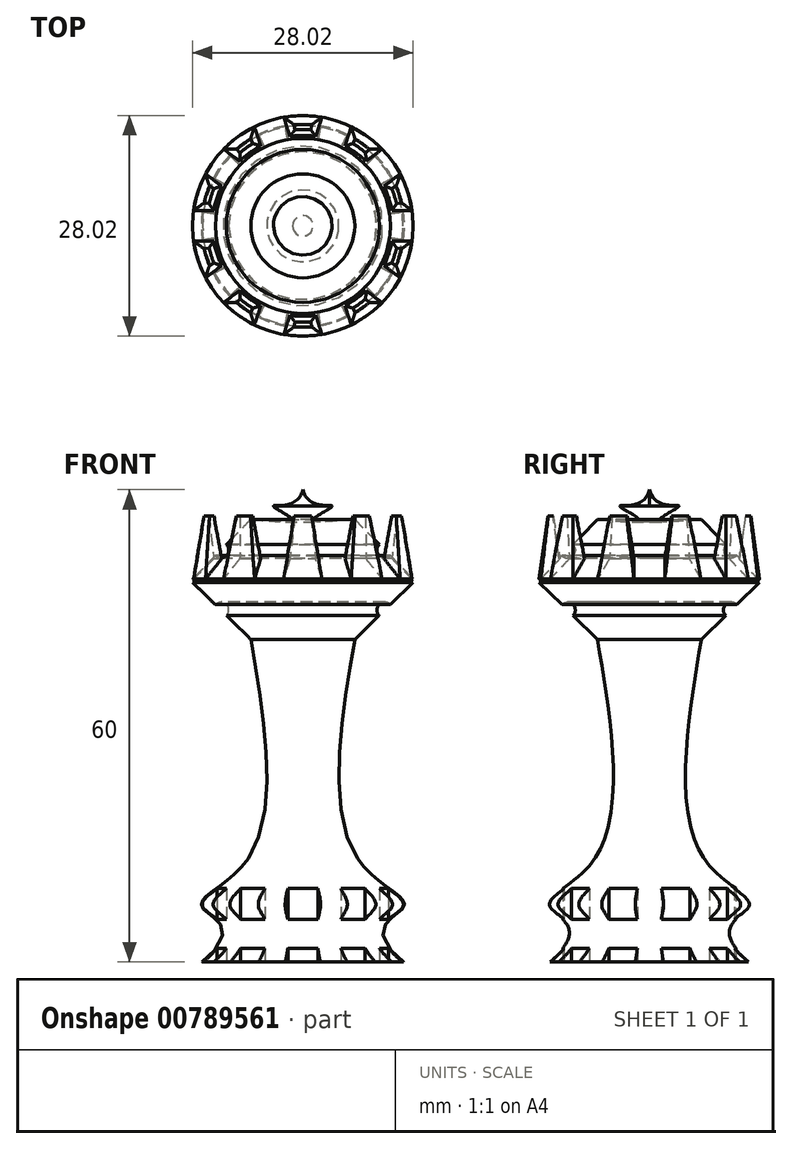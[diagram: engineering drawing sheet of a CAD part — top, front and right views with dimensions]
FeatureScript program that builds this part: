
annotation { "Feature Type Name" : "Feature", "Feature Type Description" : "" }
export const myFeature = defineFeature(function(context is Context, id is Id, definition is map)
    precondition{}
    {
        {
            var Q0;
            Q0=qCreatedBy(makeId("Front.planeOp"),FACE);
            var sketch = newSketch(context, id + "F0", { "sketchPlane" : qUnion([Q0])});
            skLineSegment(sketch, "E0", {"start": v(0, 0) * mm, "end": v(0, 60) * mm});
            skLineSegment(sketch, "E1", {"start": v(-2.2, 0) * mm, "end": v(12.8, 0) * mm});
            skFitSpline(sketch, "E2", {"points": [v(12.8, 0) * mm, v(12.8, 6.96) * mm, v(7.52, 12.35) * mm, v(6.6, 41) * mm], "startDerivative": vector(-68.04, 55.14) * mm, "endDerivative": vector(13.36, 76.17) * mm});
            skLineSegment(sketch, "E3", {"start": v(6.6, 41) * mm, "end": v(11.13, 45.4) * mm});
            skLineSegment(sketch, "E4", {"start": v(14.01, 48.63) * mm, "end": v(6.6, 56.23) * mm});
            skCircle(sketch, "E5", {"center": v(10.41, 52.32) * mm, "radius": 1 * mm});
            skCircle(sketch, "E6", {"center": v(10.41, 44.7) * mm, "radius": 1 * mm});
            skLineSegment(sketch, "E7", {"start": v(14.01, 48.63) * mm, "end": v(12.73, 48.41) * mm});
            skLineSegment(sketch, "E8", {"start": v(12.73, 48.41) * mm, "end": v(14, 48.2) * mm});
            skPoint(sketch, "E9.orphan", {"position": v(14.22, 48.41) * mm});
            skLineSegment(sketch, "E10", {"start": v(14, 48.2) * mm, "end": v(11.13, 45.4) * mm});
            skFitSpline(sketch, "E11", {"points": [v(3.74, 57.92) * mm, v(4.88, 57.03) * mm, v(3.83, 56) * mm], "startDerivative": vector(3.37, -1.72) * mm, "endDerivative": vector(-3.17, -2.1) * mm});
            skFitSpline(sketch, "E12.trimOffspring", {"points": [v(6.6, 56.23) * mm, v(1.34, 56.23) * mm, v(3.74, 57.92) * mm, v(0, 60) * mm], "startDerivative": vector(-22.01, -1.8) * mm, "endDerivative": vector(-5.75, 23.43) * mm});
            skFitSpline(sketch, "E13", {"points": [v(4.7, 56.66) * mm, v(5.56, 56.61) * mm, v(6.6, 56.23) * mm], "startDerivative": vector(1.82, 0.06) * mm, "endDerivative": vector(2, -0.89) * mm});
            skSolve(sketch);
        }
        {
            var Q0;
            {var subQ2=sQuery(id+"F0.wireOp",EDGE,"E0");Q0=makeQuery(id+"F0.imprint","IMPRINT",FACE,{"disambiguationData":[TD([[makeQuery(id+"F0.imprint","IMPRINT",EDGE,{"derivedFrom":subQ2}),-1.0]])]});}
            var Q1;
            Q1=sQuery(id+"F0.wireOp",EDGE,"E0");
            revolve(context, id + "F1", {"surfaceOperationType" : NewSurfaceOperationType.NEW, "entities" : qUnion([Q0]), "axis" : qUnion([Q1]), "revolveType" : RevolveType.FULL});
        }
        {
            var Q0;
            Q0=qCreatedBy(makeId("Top.planeOp"),FACE);
            var sketch = newSketch(context, id + "F2", { "sketchPlane" : qUnion([Q0])});
            skLineSegment(sketch, "E14", {"start": v(2.43, -13.79) * mm, "end": v(1.91, -10.83) * mm});
            skLineSegment(sketch, "E15", {"start": v(-1.91, -10.83) * mm, "end": v(-2.43, -13.79) * mm});
            skArc(sketch, "E16", {"start": v(-2.43, -13.79) * mm, "mid": v(0, -14) * mm, "end": v(2.43, -13.79) * mm});
            skArc(sketch, "E17", {"start": v(-1.91, -10.83) * mm, "mid": v(0, -11) * mm, "end": v(1.91, -10.83) * mm});
            skPoint(sketch, "E18.orphan", {"position": v(0, -22.16) * mm});
            skPoint(sketch, "E19.orphan", {"position": v(-3.9, -22.16) * mm});
            skArc(sketch, "E20.1.0", {"start": v(6.14, -12.58) * mm, "mid": v(8.23, -11.33) * mm, "end": v(10.07, -9.73) * mm});
            skLineSegment(sketch, "E20.1.1", {"start": v(4.82, -9.89) * mm, "end": v(6.14, -12.58) * mm});
            skArc(sketch, "E20.1.2", {"start": v(4.82, -9.89) * mm, "mid": v(6.47, -8.9) * mm, "end": v(7.91, -7.64) * mm});
            skLineSegment(sketch, "E20.1.3", {"start": v(10.07, -9.73) * mm, "end": v(7.91, -7.64) * mm});
            skArc(sketch, "E20.2.0", {"start": v(12.36, -6.57) * mm, "mid": v(13.31, -4.33) * mm, "end": v(13.86, -1.95) * mm});
            skLineSegment(sketch, "E20.2.1", {"start": v(9.71, -5.16) * mm, "end": v(12.36, -6.57) * mm});
            skArc(sketch, "E20.2.2", {"start": v(9.71, -5.16) * mm, "mid": v(10.46, -3.4) * mm, "end": v(10.9, -1.53) * mm});
            skLineSegment(sketch, "E20.2.3", {"start": v(13.86, -1.95) * mm, "end": v(10.9, -1.53) * mm});
            skArc(sketch, "E20.3.0", {"start": v(13.86, 1.95) * mm, "mid": v(13.31, 4.33) * mm, "end": v(12.36, 6.57) * mm});
            skLineSegment(sketch, "E20.3.1", {"start": v(10.9, 1.53) * mm, "end": v(13.86, 1.95) * mm});
            skArc(sketch, "E20.3.2", {"start": v(10.9, 1.53) * mm, "mid": v(10.46, 3.4) * mm, "end": v(9.71, 5.16) * mm});
            skLineSegment(sketch, "E20.3.3", {"start": v(12.36, 6.57) * mm, "end": v(9.71, 5.16) * mm});
            skArc(sketch, "E20.4.0", {"start": v(10.07, 9.73) * mm, "mid": v(8.23, 11.33) * mm, "end": v(6.14, 12.58) * mm});
            skLineSegment(sketch, "E20.4.1", {"start": v(7.91, 7.64) * mm, "end": v(10.07, 9.73) * mm});
            skArc(sketch, "E20.4.2", {"start": v(7.91, 7.64) * mm, "mid": v(6.47, 8.9) * mm, "end": v(4.82, 9.89) * mm});
            skLineSegment(sketch, "E20.4.3", {"start": v(6.14, 12.58) * mm, "end": v(4.82, 9.89) * mm});
            skArc(sketch, "E20.5.0", {"start": v(2.43, 13.79) * mm, "mid": v(0, 14) * mm, "end": v(-2.43, 13.79) * mm});
            skLineSegment(sketch, "E20.5.1", {"start": v(1.91, 10.83) * mm, "end": v(2.43, 13.79) * mm});
            skArc(sketch, "E20.5.2", {"start": v(1.91, 10.83) * mm, "mid": v(0, 11) * mm, "end": v(-1.91, 10.83) * mm});
            skLineSegment(sketch, "E20.5.3", {"start": v(-2.43, 13.79) * mm, "end": v(-1.91, 10.83) * mm});
            skArc(sketch, "E20.6.0", {"start": v(-6.14, 12.58) * mm, "mid": v(-8.23, 11.33) * mm, "end": v(-10.07, 9.73) * mm});
            skLineSegment(sketch, "E20.6.1", {"start": v(-4.82, 9.89) * mm, "end": v(-6.14, 12.58) * mm});
            skArc(sketch, "E20.6.2", {"start": v(-4.82, 9.89) * mm, "mid": v(-6.47, 8.9) * mm, "end": v(-7.91, 7.64) * mm});
            skLineSegment(sketch, "E20.6.3", {"start": v(-10.07, 9.73) * mm, "end": v(-7.91, 7.64) * mm});
            skArc(sketch, "E20.7.0", {"start": v(-12.36, 6.57) * mm, "mid": v(-13.31, 4.33) * mm, "end": v(-13.86, 1.95) * mm});
            skLineSegment(sketch, "E20.7.1", {"start": v(-9.71, 5.16) * mm, "end": v(-12.36, 6.57) * mm});
            skArc(sketch, "E20.7.2", {"start": v(-9.71, 5.16) * mm, "mid": v(-10.46, 3.4) * mm, "end": v(-10.9, 1.53) * mm});
            skLineSegment(sketch, "E20.7.3", {"start": v(-13.86, 1.95) * mm, "end": v(-10.9, 1.53) * mm});
            skArc(sketch, "E20.8.0", {"start": v(-13.86, -1.95) * mm, "mid": v(-13.31, -4.33) * mm, "end": v(-12.36, -6.57) * mm});
            skLineSegment(sketch, "E20.8.1", {"start": v(-10.9, -1.53) * mm, "end": v(-13.86, -1.95) * mm});
            skArc(sketch, "E20.8.2", {"start": v(-10.9, -1.53) * mm, "mid": v(-10.46, -3.4) * mm, "end": v(-9.71, -5.16) * mm});
            skLineSegment(sketch, "E20.8.3", {"start": v(-12.36, -6.57) * mm, "end": v(-9.71, -5.16) * mm});
            skArc(sketch, "E20.9.0", {"start": v(-10.07, -9.73) * mm, "mid": v(-8.23, -11.33) * mm, "end": v(-6.14, -12.58) * mm});
            skLineSegment(sketch, "E20.9.1", {"start": v(-7.91, -7.64) * mm, "end": v(-10.07, -9.73) * mm});
            skArc(sketch, "E20.9.2", {"start": v(-7.91, -7.64) * mm, "mid": v(-6.47, -8.9) * mm, "end": v(-4.82, -9.89) * mm});
            skLineSegment(sketch, "E20.9.3", {"start": v(-6.14, -12.58) * mm, "end": v(-4.82, -9.89) * mm});
            skSolve(sketch);
        }
        {
            var Q0;
            Q0=qCreatedBy(makeId("Top.planeOp"),FACE);
            cPlane(context, id + "F3", {"entities" : qUnion([Q0]), "cplaneType" : CPlaneType.OFFSET, "offset" : 48.62 * mm, "width" : 150 * mm, "height" : 150 * mm});
        }
        {
            var Q0;
            Q0=qCreatedBy(id+"F3.planeOp",FACE);
            var sketch = newSketch(context, id + "F4", { "sketchPlane" : qUnion([Q0])});
            skArc(sketch, "E21", {"start": v(2.43, 13.79) * mm, "mid": v(0, 14) * mm, "end": v(-2.43, 13.79) * mm});
            skArc(sketch, "E22", {"start": v(1.93, 10.94) * mm, "mid": v(0, 11.11) * mm, "end": v(-1.93, 10.94) * mm});
            skLineSegment(sketch, "E23", {"start": v(2.43, 13.79) * mm, "end": v(1.93, 10.94) * mm});
            skLineSegment(sketch, "E24", {"start": v(-1.93, 10.94) * mm, "end": v(-2.43, 13.79) * mm});
            skPoint(sketch, "E25.orphan", {"position": v(0, 20.43) * mm});
            skPoint(sketch, "E26.orphan", {"position": v(-3.6, 20.43) * mm});
            skArc(sketch, "E27.1.0", {"start": v(-6.14, 12.58) * mm, "mid": v(-8.23, 11.33) * mm, "end": v(-10.07, 9.73) * mm});
            skArc(sketch, "E27.1.1", {"start": v(-4.87, 9.99) * mm, "mid": v(-6.53, 9) * mm, "end": v(-8, 7.72) * mm});
            skLineSegment(sketch, "E27.1.2", {"start": v(-8, 7.72) * mm, "end": v(-10.07, 9.73) * mm});
            skLineSegment(sketch, "E27.1.3", {"start": v(-6.14, 12.58) * mm, "end": v(-4.87, 9.99) * mm});
            skArc(sketch, "E27.2.0", {"start": v(-12.36, 6.57) * mm, "mid": v(-13.31, 4.33) * mm, "end": v(-13.86, 1.95) * mm});
            skArc(sketch, "E27.2.1", {"start": v(-9.81, 5.22) * mm, "mid": v(-10.57, 3.43) * mm, "end": v(-11, 1.55) * mm});
            skLineSegment(sketch, "E27.2.2", {"start": v(-11, 1.55) * mm, "end": v(-13.86, 1.95) * mm});
            skLineSegment(sketch, "E27.2.3", {"start": v(-12.36, 6.57) * mm, "end": v(-9.81, 5.22) * mm});
            skArc(sketch, "E27.3.0", {"start": v(-13.86, -1.95) * mm, "mid": v(-13.31, -4.33) * mm, "end": v(-12.36, -6.57) * mm});
            skArc(sketch, "E27.3.1", {"start": v(-11, -1.55) * mm, "mid": v(-10.57, -3.43) * mm, "end": v(-9.81, -5.22) * mm});
            skLineSegment(sketch, "E27.3.2", {"start": v(-9.81, -5.22) * mm, "end": v(-12.36, -6.57) * mm});
            skLineSegment(sketch, "E27.3.3", {"start": v(-13.86, -1.95) * mm, "end": v(-11, -1.55) * mm});
            skArc(sketch, "E27.4.0", {"start": v(-10.07, -9.73) * mm, "mid": v(-8.23, -11.33) * mm, "end": v(-6.14, -12.58) * mm});
            skArc(sketch, "E27.4.1", {"start": v(-8, -7.72) * mm, "mid": v(-6.53, -9) * mm, "end": v(-4.87, -9.99) * mm});
            skLineSegment(sketch, "E27.4.2", {"start": v(-4.87, -9.99) * mm, "end": v(-6.14, -12.58) * mm});
            skLineSegment(sketch, "E27.4.3", {"start": v(-10.07, -9.73) * mm, "end": v(-8, -7.72) * mm});
            skArc(sketch, "E27.5.0", {"start": v(-2.43, -13.79) * mm, "mid": v(0, -14) * mm, "end": v(2.43, -13.79) * mm});
            skArc(sketch, "E27.5.1", {"start": v(-1.93, -10.94) * mm, "mid": v(0, -11.11) * mm, "end": v(1.93, -10.94) * mm});
            skLineSegment(sketch, "E27.5.2", {"start": v(1.93, -10.94) * mm, "end": v(2.43, -13.79) * mm});
            skLineSegment(sketch, "E27.5.3", {"start": v(-2.43, -13.79) * mm, "end": v(-1.93, -10.94) * mm});
            skArc(sketch, "E27.6.0", {"start": v(6.14, -12.58) * mm, "mid": v(8.23, -11.33) * mm, "end": v(10.07, -9.73) * mm});
            skArc(sketch, "E27.6.1", {"start": v(4.87, -9.99) * mm, "mid": v(6.53, -9) * mm, "end": v(8, -7.72) * mm});
            skLineSegment(sketch, "E27.6.2", {"start": v(8, -7.72) * mm, "end": v(10.07, -9.73) * mm});
            skLineSegment(sketch, "E27.6.3", {"start": v(6.14, -12.58) * mm, "end": v(4.87, -9.99) * mm});
            skArc(sketch, "E27.7.0", {"start": v(12.36, -6.57) * mm, "mid": v(13.31, -4.33) * mm, "end": v(13.86, -1.95) * mm});
            skArc(sketch, "E27.7.1", {"start": v(9.81, -5.22) * mm, "mid": v(10.57, -3.43) * mm, "end": v(11, -1.55) * mm});
            skLineSegment(sketch, "E27.7.2", {"start": v(11, -1.55) * mm, "end": v(13.86, -1.95) * mm});
            skLineSegment(sketch, "E27.7.3", {"start": v(12.36, -6.57) * mm, "end": v(9.81, -5.22) * mm});
            skArc(sketch, "E27.8.0", {"start": v(13.86, 1.95) * mm, "mid": v(13.31, 4.33) * mm, "end": v(12.36, 6.57) * mm});
            skArc(sketch, "E27.8.1", {"start": v(11, 1.55) * mm, "mid": v(10.57, 3.43) * mm, "end": v(9.81, 5.22) * mm});
            skLineSegment(sketch, "E27.8.2", {"start": v(9.81, 5.22) * mm, "end": v(12.36, 6.57) * mm});
            skLineSegment(sketch, "E27.8.3", {"start": v(13.86, 1.95) * mm, "end": v(11, 1.55) * mm});
            skArc(sketch, "E27.9.0", {"start": v(10.07, 9.73) * mm, "mid": v(8.23, 11.33) * mm, "end": v(6.14, 12.58) * mm});
            skArc(sketch, "E27.9.1", {"start": v(8, 7.72) * mm, "mid": v(6.53, 9) * mm, "end": v(4.87, 9.99) * mm});
            skLineSegment(sketch, "E27.9.2", {"start": v(4.87, 9.99) * mm, "end": v(6.14, 12.58) * mm});
            skLineSegment(sketch, "E27.9.3", {"start": v(10.07, 9.73) * mm, "end": v(8, 7.72) * mm});
            skSolve(sketch);
        }
        {
            var Q0;
            Q0 = qSketchRegion(id + "F4", true);
            extrude(context, id + "F5", {"entities" : qUnion([Q0]), "operationType" : NewBodyOperationType.ADD, "depth" : 8 * mm, "offsetDistance" : 25 * mm, "hasDraft" : true, "draftAngle" : 8 * degree, "draftPullDirection" : true});
        }
        {
            var Q0;
            Q0 = qSketchRegion(id + "F2", true);
            extrude(context, id + "F6", {"entities" : qUnion([Q0]), "operationType" : NewBodyOperationType.REMOVE, "oppositeDirection" : true, "depth" : -10 * mm, "offsetDistance" : 25 * mm});
        }
    });
